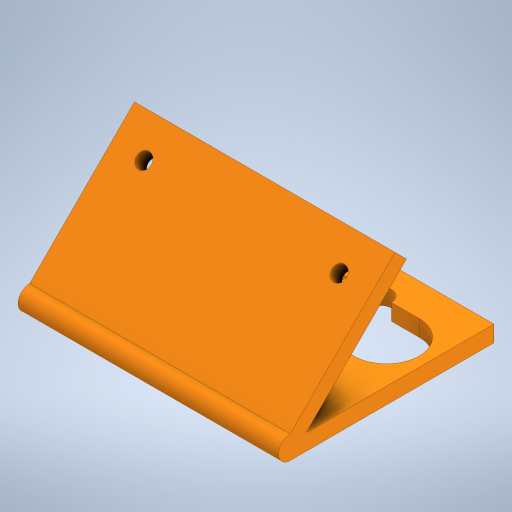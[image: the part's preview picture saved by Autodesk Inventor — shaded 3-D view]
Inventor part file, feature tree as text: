
AUTODESK INVENTOR PART (.ipt)
format: ipt  version: 2023 (Build 270158000, 158)  size: 337,408 bytes
history: native  units: mm
features: extrude x5, sketch x5
ambient origin geometry x8: Origin, YZ Plane, XZ Plane, XY Plane, X Axis, Y Axis, Z Axis, Center Point
bodies: Solid1 (feature_tree)
feature tree (10):
  extrude  "Extrusion1"  Depth=20.0mm
  extrude  "Extrusion2"  Depth=21.0mm
  extrude  "Extrusion3"  Depth=12.5mm
  extrude  "Extrusion4"  Depth=2.5mm
  extrude  "Extrusion5"  Depth=2.5mm
  sketch  "Sketch1"  dims[d0=20.0mm d1=20.0mm]
  sketch  "Sketch2"  dims[d2=54.0mm d3=21.0mm]
  sketch  "Sketch3"  dims[d4=12.5mm d5=12.5mm]
  sketch  "Sketch4"  dims[d6=21.0mm d7=2.5mm]
  sketch  "Sketch5"  dims[d8=2.5mm d9=2.5mm d10=2.5mm d11=5.0mm d12=5.0mm d13=5.0mm d14=5.0mm d15=11.0mm d16=11.0mm d17=40.0mm d18=80.0mm d19=13.0mm d20=20.0mm d21=5.0mm d22=0.0mm d23=45.0deg d24=5.0mm d25=5.0mm d26=80.0mm d27=0.0mm d28=30.0mm d29=10.0mm d30=25.0mm d31=10.0mm d32=80.0mm d33=0.0mm d34=10.0mm d35=10.0mm d36=4.5mm d37=10.0mm d38=10.0mm d39=4.5mm d40=80.0mm d41=0.0mm d42=7.0mm d43=7.0mm d44=7.0mm d45=7.0mm d46=20.0mm d47=0.0mm d48=20.0mm d49=0.0mm d50=6.0mm d51=0.0mm]
